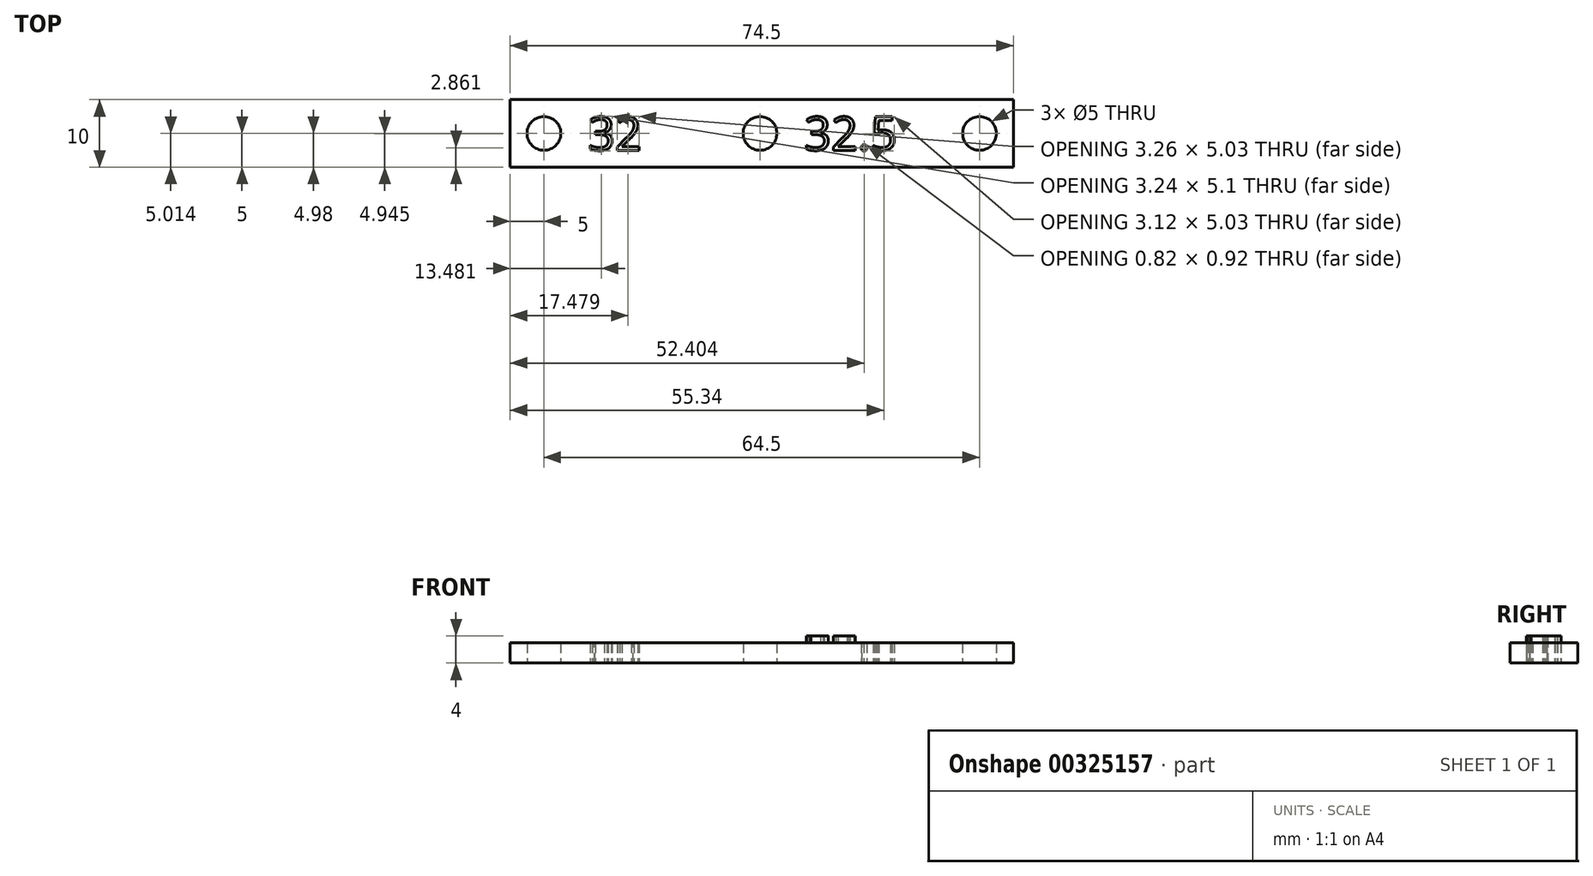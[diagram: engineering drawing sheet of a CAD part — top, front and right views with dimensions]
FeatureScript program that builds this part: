
annotation { "Feature Type Name" : "Feature", "Feature Type Description" : "" }
export const myFeature = defineFeature(function(context is Context, id is Id, definition is map)
    precondition{}
    {
        {
            var Q0;
            Q0=qCreatedBy(makeId("Top.planeOp"),FACE);
            var sketch = newSketch(context, id + "F0", { "sketchPlane" : qUnion([Q0])});
            skLineSegment(sketch, "E0", {"start": v(0, 0) * mm, "end": v(32.5, 0) * mm, "construction": true});
            skText(sketch, "E1", { "text": "32.5", "fontName": "OpenSans-Regular.ttf"});
            skCircle(sketch, "E2", {"center": v(0, 0) * mm, "radius": 2.5 * mm});
            skCircle(sketch, "E3", {"center": v(32.5, 0) * mm, "radius": 2.5 * mm});
            skLineSegment(sketch, "E4", {"start": v(0, 0) * mm, "end": v(-32, 0) * mm, "construction": true});
            skLineSegment(sketch, "E5", {"start": v(-32, 0) * mm, "end": v(-37, 0) * mm, "construction": true});
            skText(sketch, "E6", { "text": "32", "fontName": "OpenSans-Regular.ttf"});
            skLineSegment(sketch, "E7", {"start": v(0, 0) * mm, "end": v(6.54, 2.5) * mm, "construction": true});
            skLineSegment(sketch, "E8", {"start": v(0, 0) * mm, "end": v(6.54, -2.5) * mm, "construction": true});
            skLineSegment(sketch, "E9", {"start": v(-32, 0) * mm, "end": v(-25.46, 2.5) * mm, "construction": true});
            skLineSegment(sketch, "E10", {"start": v(-25.46, -2.5) * mm, "end": v(-32, 0) * mm, "construction": true});
            skCircle(sketch, "E11", {"center": v(-32, 0) * mm, "radius": 2.5 * mm});
            skLineSegment(sketch, "E12", {"start": v(-37, 0) * mm, "end": v(-37, 5) * mm});
            skLineSegment(sketch, "E13", {"start": v(-37, 0) * mm, "end": v(-37, -5) * mm});
            skLineSegment(sketch, "E14", {"start": v(32.5, 0) * mm, "end": v(37.5, 0) * mm, "construction": true});
            skLineSegment(sketch, "E15", {"start": v(37.5, 0) * mm, "end": v(37.5, 5) * mm});
            skLineSegment(sketch, "E16", {"start": v(37.5, 0) * mm, "end": v(37.5, -5) * mm});
            skLineSegment(sketch, "E17", {"start": v(37.5, 5) * mm, "end": v(-37, 5) * mm});
            skLineSegment(sketch, "E18", {"start": v(-37, -5) * mm, "end": v(37.5, -5) * mm});
            const initialGuessF0  = {"E1": [0.00654, -0.0025, 1, 0, 0.005], "E6": [-0.02546, -0.0025, 1, 0, 0.005]};
            skSetInitialGuess(sketch, initialGuessF0);
            skSolve(sketch);
        }
        {
            var Q0;
            Q0=makeQuery(id+"F0.imprint","IMPRINT",FACE,{"disambiguationData":[TD([[makeQuery(id+"F0.imprint","IMPRINT",EDGE,{"derivedFrom":sQuery(id+"F0.wireOp",EDGE,"E1.sketch_text.stroke-0")}),1.0]])]});
            extrude(context, id + "F1", {"entities" : qUnion([Q0]), "depth" : 3 * mm});
        }
        {
            var Q0;
            Q0=makeQuery(id+"F0.imprint","IMPRINT",FACE,{"disambiguationData":[TD([[makeQuery(id+"F0.imprint","IMPRINT",EDGE,{"derivedFrom":sQuery(id+"F0.wireOp",EDGE,"E1.sketch_text.stroke-0")}),-1.0]])]});
            var Q1;
            Q1=makeQuery(id+"F0.imprint","IMPRINT",FACE,{"disambiguationData":[TD([[makeQuery(id+"F0.imprint","IMPRINT",EDGE,{"derivedFrom":sQuery(id+"F0.wireOp",EDGE,"E1.sketch_text.stroke-27")}),-1.0]])]});
            var Q2;
            Q2=makeQuery(id+"F0.imprint","IMPRINT",FACE,{"disambiguationData":[TD([[makeQuery(id+"F0.imprint","IMPRINT",EDGE,{"derivedFrom":sQuery(id+"F0.wireOp",EDGE,"E1.sketch_text.stroke-35")}),-1.0]])]});
            var Q3;
            Q3=makeQuery(id+"F0.imprint","IMPRINT",FACE,{"disambiguationData":[TD([[makeQuery(id+"F0.imprint","IMPRINT",EDGE,{"derivedFrom":sQuery(id+"F0.wireOp",EDGE,"E1.sketch_text.stroke-20")}),-1.0]])]});
            extrude(context, id + "F2", {"entities" : qUnion([Q0, Q1, Q2, Q3]), "operationType" : NewBodyOperationType.ADD, "depth" : 4 * mm});
        }
    });
